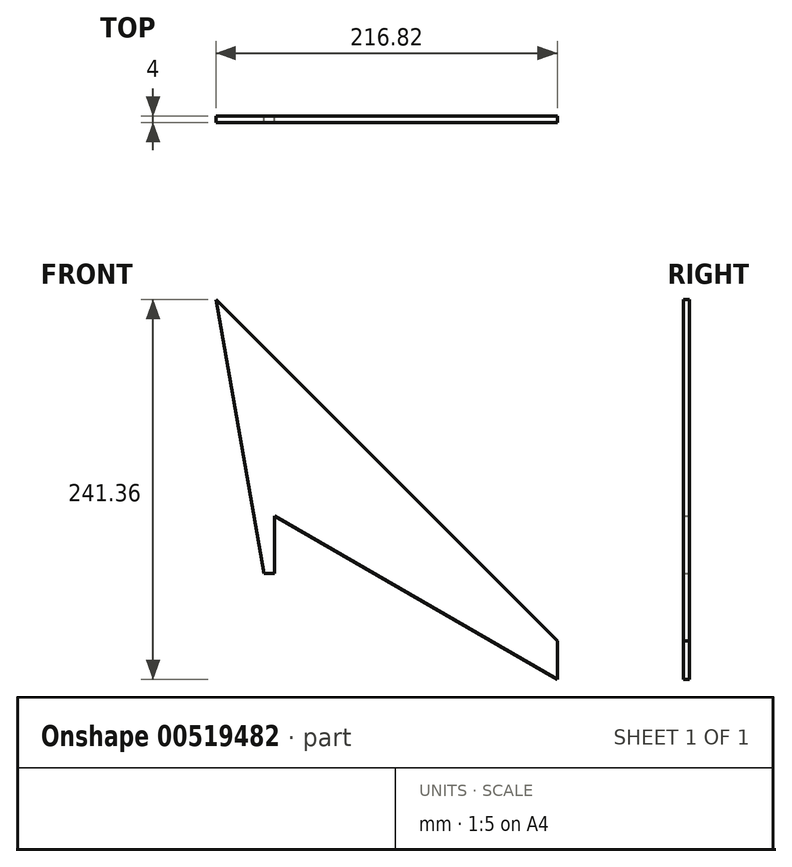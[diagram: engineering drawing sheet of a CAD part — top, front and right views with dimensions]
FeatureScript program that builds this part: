
annotation { "Feature Type Name" : "Feature", "Feature Type Description" : "" }
export const myFeature = defineFeature(function(context is Context, id is Id, definition is map)
    precondition{}
    {
        {
            var Q0;
            Q0=qCreatedBy(makeId("Front.planeOp"),FACE);
            var sketch = newSketch(context, id + "F0", { "sketchPlane" : qUnion([Q0])});
            skLineSegment(sketch, "E0", {"start": v(0, 36.48) * mm, "end": v(0, 72.96) * mm});
            skLineSegment(sketch, "E1", {"start": v(0, 72.96) * mm, "end": v(179.69, -30.78) * mm});
            skLineSegment(sketch, "E2", {"start": v(179.69, -6.23) * mm, "end": v(-37.13, 210.58) * mm});
            skLineSegment(sketch, "E3", {"start": v(-37.13, 210.58) * mm, "end": v(-6.43, 36.48) * mm});
            skLineSegment(sketch, "E4", {"start": v(179.69, -30.78) * mm, "end": v(179.69, -6.23) * mm});
            skLineSegment(sketch, "E5", {"start": v(-6.43, 36.48) * mm, "end": v(0, 36.48) * mm});
            skPoint(sketch, "E5.startSnap0", {"position": v(0, 36.48) * mm});
            skPoint(sketch, "E6.orphan", {"position": v(0, 0) * mm});
            skSolve(sketch);
        }
        {
            var Q0;
            Q0=makeQuery(id+"F0.imprint","IMPRINT",FACE,{"disambiguationData":[TD([[makeQuery(id+"F0.imprint","IMPRINT",EDGE,{"derivedFrom":sQuery(id+"F0.wireOp",EDGE,"E0")}),1.0]])]});
            extrude(context, id + "F1", {"entities" : qUnion([Q0]), "depth" : 4 * mm, "offsetDistance" : 25 * mm});
        }
    });
